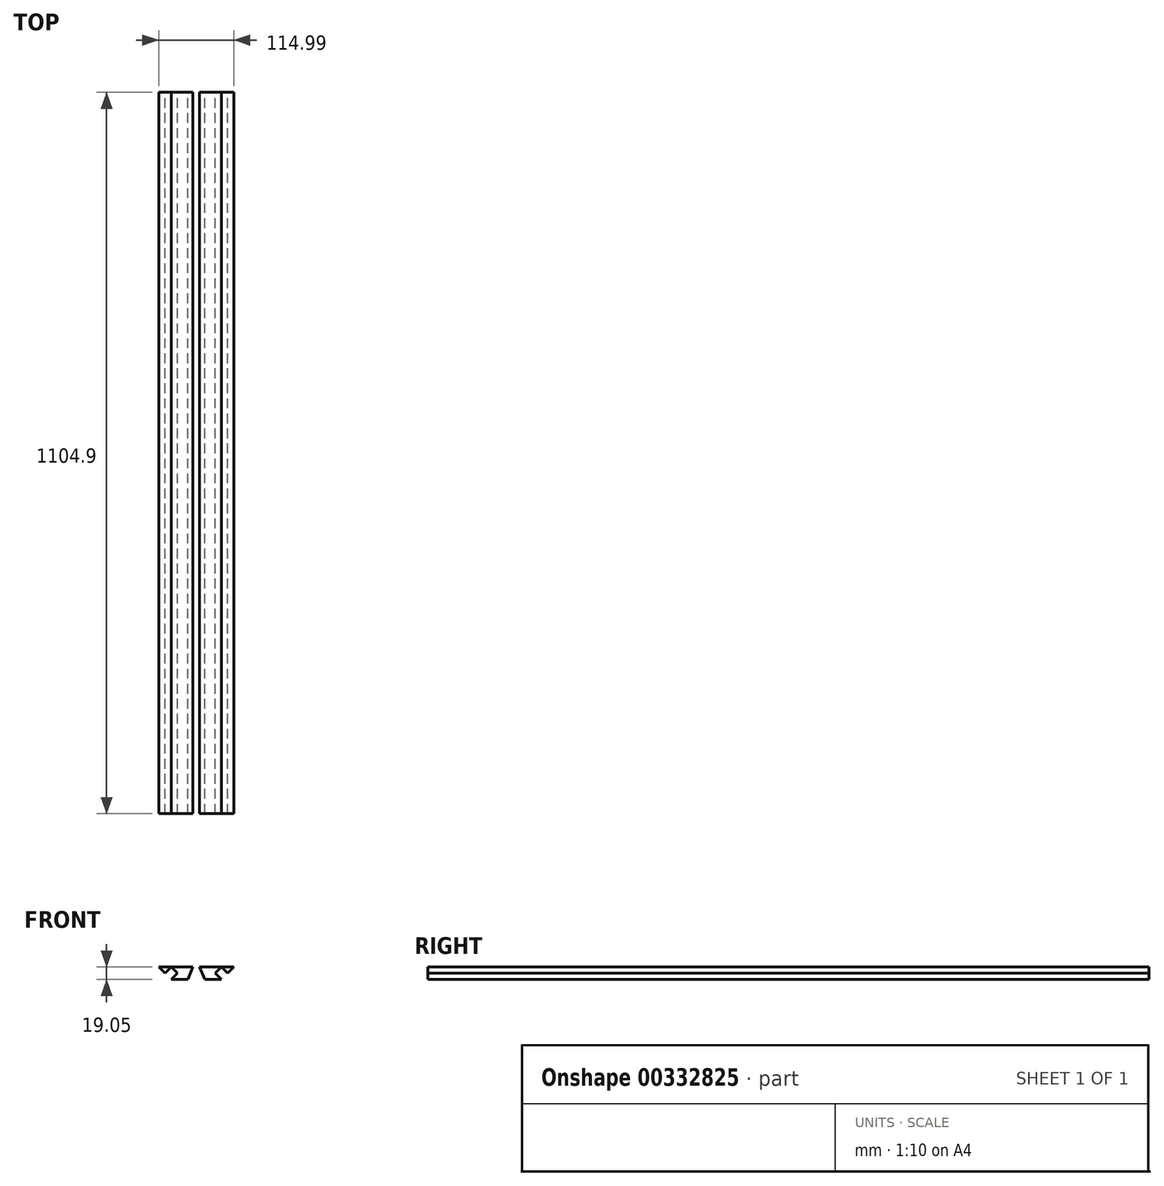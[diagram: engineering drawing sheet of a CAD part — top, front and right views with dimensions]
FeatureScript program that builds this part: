
annotation { "Feature Type Name" : "Feature", "Feature Type Description" : "" }
export const myFeature = defineFeature(function(context is Context, id is Id, definition is map)
    precondition{}
    {
        {
            var Q0;
            Q0=qCreatedBy(makeId("Front.planeOp"),FACE);
            var sketch = newSketch(context, id + "F0", { "sketchPlane" : qUnion([Q0])});
            skLineSegment(sketch, "E0.bottom", {"start": v(19.05, 0) * mm, "end": v(44.45, 0) * mm});
            skLineSegment(sketch, "E0.top", {"start": v(0, 19.05) * mm, "end": v(52.34, 19.05) * mm});
            skLineSegment(sketch, "E1", {"start": v(0, 19.05) * mm, "end": v(9.53, 9.53) * mm});
            skLineSegment(sketch, "E2", {"start": v(9.52, 9.52) * mm, "end": v(19.05, 19.05) * mm});
            skLineSegment(sketch, "E3", {"start": v(19.05, 19.05) * mm, "end": v(28.58, 9.53) * mm});
            skLineSegment(sketch, "E4", {"start": v(19.05, 0) * mm, "end": v(28.58, 9.53) * mm});
            skLineSegment(sketch, "E5", {"start": v(44.45, 0) * mm, "end": v(52.34, 19.05) * mm});
            skLineSegment(sketch, "E6", {"start": v(57.5, 19.05) * mm, "end": v(49.6, 0) * mm});
            skLineSegment(sketch, "E7", {"start": v(57.5, 19.05) * mm, "end": v(57.5, -46.96) * mm, "construction": true});
            skLineSegment(sketch, "E8.MirrorCS", {"start": v(115, 19.05) * mm, "end": v(62.65, 19.05) * mm});
            skLineSegment(sketch, "E9.MirrorCS", {"start": v(70.54, 0) * mm, "end": v(62.65, 19.05) * mm});
            skLineSegment(sketch, "E10.MirrorCS", {"start": v(95.94, 0) * mm, "end": v(70.54, 0) * mm});
            skLineSegment(sketch, "E11.MirrorCS", {"start": v(95.94, 0) * mm, "end": v(86.42, 9.53) * mm});
            skLineSegment(sketch, "E12.MirrorCS", {"start": v(115, 19.05) * mm, "end": v(105.47, 9.52) * mm});
            skLineSegment(sketch, "E13.MirrorCS", {"start": v(95.94, 19.05) * mm, "end": v(86.42, 9.52) * mm});
            skLineSegment(sketch, "E14.MirrorCS", {"start": v(105.47, 9.52) * mm, "end": v(95.94, 19.05) * mm});
            skSolve(sketch);
        }
        {
            var Q0;
            Q0 = qSketchRegion(id + "F0", true);
            extrude(context, id + "F1", {"entities" : qUnion([Q0]), "depth" : 1104.9 * mm, "offsetDistance" : 25.4 * mm});
        }
    });
